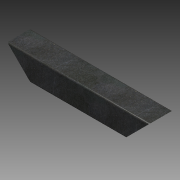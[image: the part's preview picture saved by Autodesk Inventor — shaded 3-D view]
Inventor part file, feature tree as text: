
AUTODESK INVENTOR PART (.ipt)
format: ipt  version: 2015 SP1 (Build 190203100, 203)  size: 115,712 bytes
history: native  units: in
note: dims shown in document units (in); Inventor stores cm internally (conversion verified against a paired STEP export)
features: extrude x2, sketch x2, fillet x1
ambient origin geometry x8: Origin, YZ Plane, XZ Plane, XY Plane, X Axis, Y Axis, Z Axis, Center Point
bodies: Solid1 (feature_tree)
feature tree (5):
  extrude  "Extrusion1"  Depth=2.0in
  fillet  "Fillet1"  Radius=0.083in
  extrude  "Extrusion2"  Depth=0.125in
  sketch  "Sketch1"  dims[d0=2.0in d1=2.0in d2=0.083in]
  sketch  "Sketch2"  dims[d3=12.0in d4=0.0in d5=0.125in d6=45.0deg d7=45.0deg d8=1.0in d9=0.0in]
